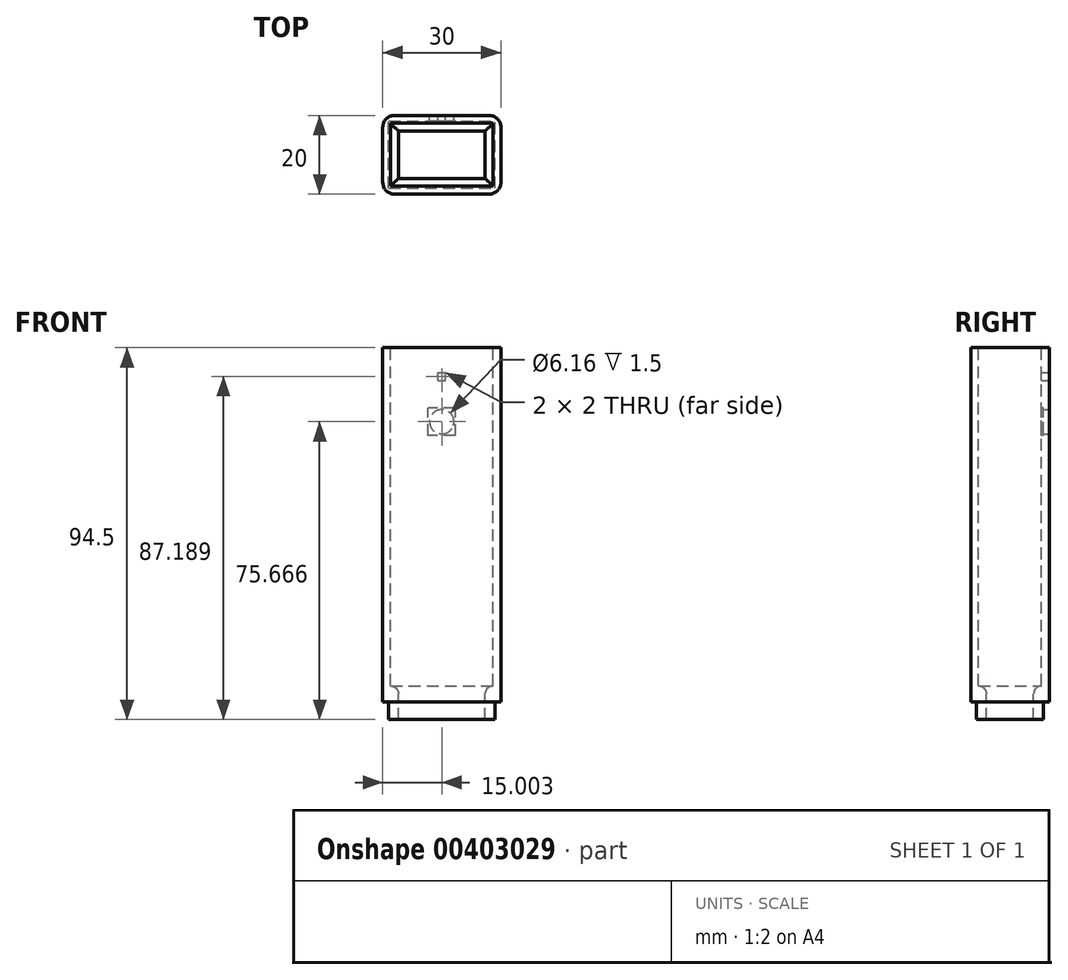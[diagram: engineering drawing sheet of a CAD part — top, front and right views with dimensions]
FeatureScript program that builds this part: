
annotation { "Feature Type Name" : "Feature", "Feature Type Description" : "" }
export const myFeature = defineFeature(function(context is Context, id is Id, definition is map)
    precondition{}
    {
        {
            var Q0;
            Q0=qCreatedBy(makeId("Top.planeOp"),FACE);
            var sketch = newSketch(context, id + "F0", { "sketchPlane" : qUnion([Q0])});
            skLineSegment(sketch, "E0.bottom", {"start": v(-19.63, 17.98) * mm, "end": v(10.37, 17.98) * mm});
            skLineSegment(sketch, "E0.top", {"start": v(-19.63, -2.02) * mm, "end": v(10.37, -2.02) * mm});
            skLineSegment(sketch, "E0.left", {"start": v(-19.63, 17.98) * mm, "end": v(-19.63, -2.02) * mm});
            skLineSegment(sketch, "E0.right", {"start": v(10.37, 17.98) * mm, "end": v(10.37, -2.02) * mm});
            skSolve(sketch);
        }
        {
            var Q0;
            Q0 = qSketchRegion(id + "F0", true);
            extrude(context, id + "F1", {"entities" : qUnion([Q0]), "depth" : 90 * mm});
        }
        {
            var Q0;
            Q0=makeQuery(id+"F1.opExtrude","SWEPT_EDGE",EDGE,{"disambiguationData":[OSD([sQuery(id+"F0.wireOp",EDGE,"E0.top"),sQuery(id+"F0.wireOp",EDGE,"E0.left")])]});
            var Q1;
            Q1=makeQuery(id+"F1.opExtrude","SWEPT_EDGE",EDGE,{"disambiguationData":[OSD([sQuery(id+"F0.wireOp",EDGE,"E0.bottom"),sQuery(id+"F0.wireOp",EDGE,"E0.left")])]});
            var Q2;
            Q2=makeQuery(id+"F1.opExtrude","SWEPT_EDGE",EDGE,{"disambiguationData":[OSD([sQuery(id+"F0.wireOp",EDGE,"E0.top"),sQuery(id+"F0.wireOp",EDGE,"E0.right")])]});
            var Q3;
            Q3=makeQuery(id+"F1.opExtrude","SWEPT_EDGE",EDGE,{"disambiguationData":[OSD([sQuery(id+"F0.wireOp",EDGE,"E0.bottom"),sQuery(id+"F0.wireOp",EDGE,"E0.right")])]});
            fillet(context, id + "F2", {"entities" : qUnion([Q0, Q1, Q2, Q3]), "radius" : 3 * mm, "tangentPropagation" : true, "allowEdgeOverflow" : false});
        }
        {
            var Q0;
            Q0=makeQuery(id+"F1.opExtrude","CAP_FACE",FACE,{"disambiguationData":[OSD([sQuery(id+"F0.wireOp",EDGE,"E0.bottom"),sQuery(id+"F0.wireOp",EDGE,"E0.top"),sQuery(id+"F0.wireOp",EDGE,"E0.left"),sQuery(id+"F0.wireOp",EDGE,"E0.right")])],"isStart":false});
            var sketch = newSketch(context, id + "F3", { "sketchPlane" : qUnion([Q0])});
            skLineSegment(sketch, "E1.bottom", {"start": v(-17.63, 15.98) * mm, "end": v(8.37, 15.98) * mm});
            skLineSegment(sketch, "E1.top", {"start": v(-17.63, -0.02) * mm, "end": v(8.37, -0.02) * mm});
            skLineSegment(sketch, "E1.left", {"start": v(-17.63, 15.98) * mm, "end": v(-17.63, -0.02) * mm});
            skLineSegment(sketch, "E1.right", {"start": v(8.37, 15.98) * mm, "end": v(8.37, -0.02) * mm});
            skSolve(sketch);
        }
        {
            var Q0;
            Q0 = qSketchRegion(id + "F3", true);
            extrude(context, id + "F4", {"entities" : qUnion([Q0]), "operationType" : NewBodyOperationType.REMOVE, "oppositeDirection" : true, "depth" : 100 * mm});
        }
        {
            var Q0;
            Q0=makeQuery(id+"F1.opExtrude","CAP_FACE",FACE,{"disambiguationData":[OSD([sQuery(id+"F0.wireOp",EDGE,"E0.bottom"),sQuery(id+"F0.wireOp",EDGE,"E0.top"),sQuery(id+"F0.wireOp",EDGE,"E0.left"),sQuery(id+"F0.wireOp",EDGE,"E0.right")])],"isStart":true});
            var sketch = newSketch(context, id + "F5", { "sketchPlane" : qUnion([Q0])});
            skLineSegment(sketch, "E2.bottom", {"start": v(-18.13, 0.52) * mm, "end": v(8.87, 0.52) * mm});
            skLineSegment(sketch, "E2.top", {"start": v(-18.13, -16.48) * mm, "end": v(8.87, -16.48) * mm});
            skLineSegment(sketch, "E2.left", {"start": v(-18.13, 0.52) * mm, "end": v(-18.13, -16.48) * mm});
            skLineSegment(sketch, "E2.right", {"start": v(8.87, 0.52) * mm, "end": v(8.87, -16.48) * mm});
            skSolve(sketch);
        }
        {
            var Q0;
            Q0 = qSketchRegion(id + "F5", true);
            extrude(context, id + "F6", {"entities" : qUnion([Q0]), "operationType" : NewBodyOperationType.ADD, "depth" : 4.5 * mm});
        }
        {
            var Q0;
            Q0=makeQuery(id+"F6.opExtrude","CAP_FACE",FACE,{"disambiguationData":[OSD([sQuery(id+"F5.wireOp",EDGE,"E2.bottom"),sQuery(id+"F5.wireOp",EDGE,"E2.top"),sQuery(id+"F5.wireOp",EDGE,"E2.left"),sQuery(id+"F5.wireOp",EDGE,"E2.right")])],"isStart":true});
            extrude(context, id + "F7", {"entities" : qUnion([Q0]), "operationType" : NewBodyOperationType.REMOVE, "oppositeDirection" : true, "depth" : 5 * mm});
        }
        {
            var Q0;
            Q0=makeQuery(id+"F1.opExtrude","SWEPT_FACE",FACE,{"disambiguationData":[OSD([sQuery(id+"F0.wireOp",EDGE,"E0.bottom")])]});
            var sketch = newSketch(context, id + "F8", { "sketchPlane" : qUnion([Q0])});
            skCircle(sketch, "E3", {"center": v(4.63, 71.17) * mm, "radius": 3.08 * mm});
            skLineSegment(sketch, "E4.bottom", {"start": v(5.63, 81.69) * mm, "end": v(3.63, 81.69) * mm});
            skLineSegment(sketch, "E4.top", {"start": v(5.63, 83.69) * mm, "end": v(3.63, 83.69) * mm});
            skLineSegment(sketch, "E4.left", {"start": v(5.63, 81.69) * mm, "end": v(5.63, 83.69) * mm});
            skLineSegment(sketch, "E4.right", {"start": v(3.63, 81.69) * mm, "end": v(3.63, 83.69) * mm});
            skSolve(sketch);
        }
        {
            var Q0;
            Q0 = qSketchRegion(id + "F8", true);
            extrude(context, id + "F9", {"entities" : qUnion([Q0]), "operationType" : NewBodyOperationType.REMOVE, "oppositeDirection" : true, "depth" : 2 * mm});
        }
        {
            var Q0;
            {var subQ0=sQuery(id+"F3.wireOp",EDGE,"E1.bottom");Q0=makeQuery(id+"F7.boolean.opBoolean","MERGE",FACE,{"derivedFrom":[makeQuery(id+"F4.boolean.opBoolean","COPY",FACE,{"derivedFrom":makeQuery(id+"F4.opExtrude","SWEPT_FACE",FACE,{"disambiguationData":[OSD([subQ0])]})}),makeQuery(id+"F7.opExtrude","SWEPT_FACE",FACE,{"disambiguationData":[OSD([sQuery(id+"F0.wireOp",EDGE,"E0.bottom"),sQuery(id+"F0.wireOp",EDGE,"E0.top"),sQuery(id+"F0.wireOp",EDGE,"E0.left"),sQuery(id+"F0.wireOp",EDGE,"E0.right"),subQ0])]})]});}
            var sketch = newSketch(context, id + "F10", { "sketchPlane" : qUnion([Q0])});
            skLineSegment(sketch, "E5.bottom", {"start": v(-1.16, 67.62) * mm, "end": v(-8.16, 67.62) * mm});
            skLineSegment(sketch, "E5.top", {"start": v(-1.16, 74.62) * mm, "end": v(-8.16, 74.62) * mm});
            skLineSegment(sketch, "E5.left", {"start": v(-1.16, 67.62) * mm, "end": v(-1.16, 74.62) * mm});
            skLineSegment(sketch, "E5.right", {"start": v(-8.16, 67.62) * mm, "end": v(-8.16, 74.62) * mm});
            skSolve(sketch);
        }
        {
            var Q0;
            Q0 = qSketchRegion(id + "F10", true);
            extrude(context, id + "F11", {"entities" : qUnion([Q0]), "operationType" : NewBodyOperationType.REMOVE, "oppositeDirection" : true, "depth" : .5 * mm});
        }
        {
            var Q0;
            {var subQ0=sQuery(id+"F3.wireOp",EDGE,"E1.bottom");Q0=makeQuery(id+"F7.boolean.opBoolean","MERGE",FACE,{"derivedFrom":[makeQuery(id+"F4.boolean.opBoolean","COPY",FACE,{"derivedFrom":makeQuery(id+"F4.opExtrude","SWEPT_FACE",FACE,{"disambiguationData":[OSD([subQ0])]})}),makeQuery(id+"F7.opExtrude","SWEPT_FACE",FACE,{"disambiguationData":[OSD([sQuery(id+"F0.wireOp",EDGE,"E0.bottom"),sQuery(id+"F0.wireOp",EDGE,"E0.top"),sQuery(id+"F0.wireOp",EDGE,"E0.left"),sQuery(id+"F0.wireOp",EDGE,"E0.right"),subQ0])]})]});}
            var sketch = newSketch(context, id + "F12", { "sketchPlane" : qUnion([Q0])});
            skLineSegment(sketch, "E6.bottom", {"start": v(-17.63, -4.5) * mm, "end": v(8.37, -4.5) * mm});
            skLineSegment(sketch, "E6.top", {"start": v(-17.63, 4.03) * mm, "end": v(8.37, 4.03) * mm});
            skLineSegment(sketch, "E6.left", {"start": v(-17.63, -4.5) * mm, "end": v(-17.63, 4.03) * mm});
            skLineSegment(sketch, "E6.right", {"start": v(8.37, -4.5) * mm, "end": v(8.37, 4.03) * mm});
            skSolve(sketch);
        }
        {
            var Q0;
            Q0 = qSketchRegion(id + "F12", true);
            extrude(context, id + "F13", {"entities" : qUnion([Q0]), "operationType" : NewBodyOperationType.ADD, "depth" : 2 * mm});
        }
        {
            var Q0;
            {var subQ0=sQuery(id+"F3.wireOp",EDGE,"E1.right");Q0=makeQuery(id+"F7.boolean.opBoolean","MERGE",FACE,{"derivedFrom":[makeQuery(id+"F4.boolean.opBoolean","COPY",FACE,{"derivedFrom":makeQuery(id+"F4.opExtrude","SWEPT_FACE",FACE,{"disambiguationData":[OSD([subQ0])]})}),makeQuery(id+"F7.opExtrude","SWEPT_FACE",FACE,{"disambiguationData":[OSD([sQuery(id+"F0.wireOp",EDGE,"E0.bottom"),sQuery(id+"F0.wireOp",EDGE,"E0.top"),sQuery(id+"F0.wireOp",EDGE,"E0.left"),sQuery(id+"F0.wireOp",EDGE,"E0.right"),subQ0])]})]});}
            var sketch = newSketch(context, id + "F14", { "sketchPlane" : qUnion([Q0])});
            skLineSegment(sketch, "E7.bottom", {"start": v(-13.98, 4.03) * mm, "end": v(0.02, 4.03) * mm});
            skLineSegment(sketch, "E7.top", {"start": v(-13.98, -4.5) * mm, "end": v(0.02, -4.5) * mm});
            skLineSegment(sketch, "E7.left", {"start": v(-13.98, 4.03) * mm, "end": v(-13.98, -4.5) * mm});
            skLineSegment(sketch, "E7.right", {"start": v(0.02, 4.03) * mm, "end": v(0.02, -4.5) * mm});
            skSolve(sketch);
        }
        {
            var Q0;
            Q0 = qSketchRegion(id + "F14", true);
            extrude(context, id + "F15", {"entities" : qUnion([Q0]), "operationType" : NewBodyOperationType.ADD, "depth" : 2 * mm});
        }
        {
            var Q0;
            {var subQ0=sQuery(id+"F3.wireOp",EDGE,"E1.top");Q0=makeQuery(id+"F7.boolean.opBoolean","MERGE",FACE,{"derivedFrom":[makeQuery(id+"F4.boolean.opBoolean","COPY",FACE,{"derivedFrom":makeQuery(id+"F4.opExtrude","SWEPT_FACE",FACE,{"disambiguationData":[OSD([subQ0])]})}),makeQuery(id+"F7.opExtrude","SWEPT_FACE",FACE,{"disambiguationData":[OSD([sQuery(id+"F0.wireOp",EDGE,"E0.bottom"),sQuery(id+"F0.wireOp",EDGE,"E0.top"),sQuery(id+"F0.wireOp",EDGE,"E0.left"),sQuery(id+"F0.wireOp",EDGE,"E0.right"),subQ0])]})]});}
            var sketch = newSketch(context, id + "F16", { "sketchPlane" : qUnion([Q0])});
            skLineSegment(sketch, "E8.bottom", {"start": v(-6.37, 4.03) * mm, "end": v(17.63, 4.03) * mm});
            skLineSegment(sketch, "E8.top", {"start": v(-6.37, -4.5) * mm, "end": v(17.63, -4.5) * mm});
            skLineSegment(sketch, "E8.left", {"start": v(-6.37, 4.03) * mm, "end": v(-6.37, -4.5) * mm});
            skLineSegment(sketch, "E8.right", {"start": v(17.63, 4.03) * mm, "end": v(17.63, -4.5) * mm});
            skSolve(sketch);
        }
        {
            var Q0;
            Q0 = qSketchRegion(id + "F16", true);
            extrude(context, id + "F17", {"entities" : qUnion([Q0]), "operationType" : NewBodyOperationType.ADD, "depth" : 2 * mm});
        }
        {
            var Q0;
            {var subQ0=sQuery(id+"F3.wireOp",EDGE,"E1.left");Q0=makeQuery(id+"F7.boolean.opBoolean","MERGE",FACE,{"derivedFrom":[makeQuery(id+"F4.boolean.opBoolean","COPY",FACE,{"derivedFrom":makeQuery(id+"F4.opExtrude","SWEPT_FACE",FACE,{"disambiguationData":[OSD([subQ0])]})}),makeQuery(id+"F7.opExtrude","SWEPT_FACE",FACE,{"disambiguationData":[OSD([sQuery(id+"F0.wireOp",EDGE,"E0.bottom"),sQuery(id+"F0.wireOp",EDGE,"E0.top"),sQuery(id+"F0.wireOp",EDGE,"E0.left"),sQuery(id+"F0.wireOp",EDGE,"E0.right"),subQ0])]})]});}
            var sketch = newSketch(context, id + "F18", { "sketchPlane" : qUnion([Q0])});
            skLineSegment(sketch, "E9.bottom", {"start": v(1.98, 4.03) * mm, "end": v(13.98, 4.03) * mm});
            skLineSegment(sketch, "E9.top", {"start": v(1.98, -4.5) * mm, "end": v(13.98, -4.5) * mm});
            skLineSegment(sketch, "E9.left", {"start": v(1.98, 4.03) * mm, "end": v(1.98, -4.5) * mm});
            skLineSegment(sketch, "E9.right", {"start": v(13.98, 4.03) * mm, "end": v(13.98, -4.5) * mm});
            skSolve(sketch);
        }
        {
            var Q0;
            Q0 = qSketchRegion(id + "F18", true);
            extrude(context, id + "F19", {"entities" : qUnion([Q0]), "operationType" : NewBodyOperationType.ADD, "depth" : 2 * mm});
        }
        {
            var Q0;
            Q0=makeQuery(id+"F19.opExtrude","CAP_EDGE",EDGE,{"disambiguationData":[OSD([sQuery(id+"F18.wireOp",EDGE,"E9.bottom")])],"isStart":false});
            var Q1;
            Q1=makeQuery(id+"F17.opExtrude","CAP_EDGE",EDGE,{"disambiguationData":[OSD([sQuery(id+"F16.wireOp",EDGE,"E8.bottom")])],"isStart":false});
            var Q2;
            Q2=makeQuery(id+"F15.opExtrude","CAP_EDGE",EDGE,{"disambiguationData":[OSD([sQuery(id+"F14.wireOp",EDGE,"E7.bottom")])],"isStart":false});
            var Q3;
            Q3=makeQuery(id+"F13.opExtrude","CAP_EDGE",EDGE,{"disambiguationData":[OSD([sQuery(id+"F12.wireOp",EDGE,"E6.top")])],"isStart":false});
            fillet(context, id + "F20", {"entities" : qUnion([Q0, Q1, Q2, Q3]), "radius" : 2 * mm, "tangentPropagation" : true, "allowEdgeOverflow" : false});
        }
    });
